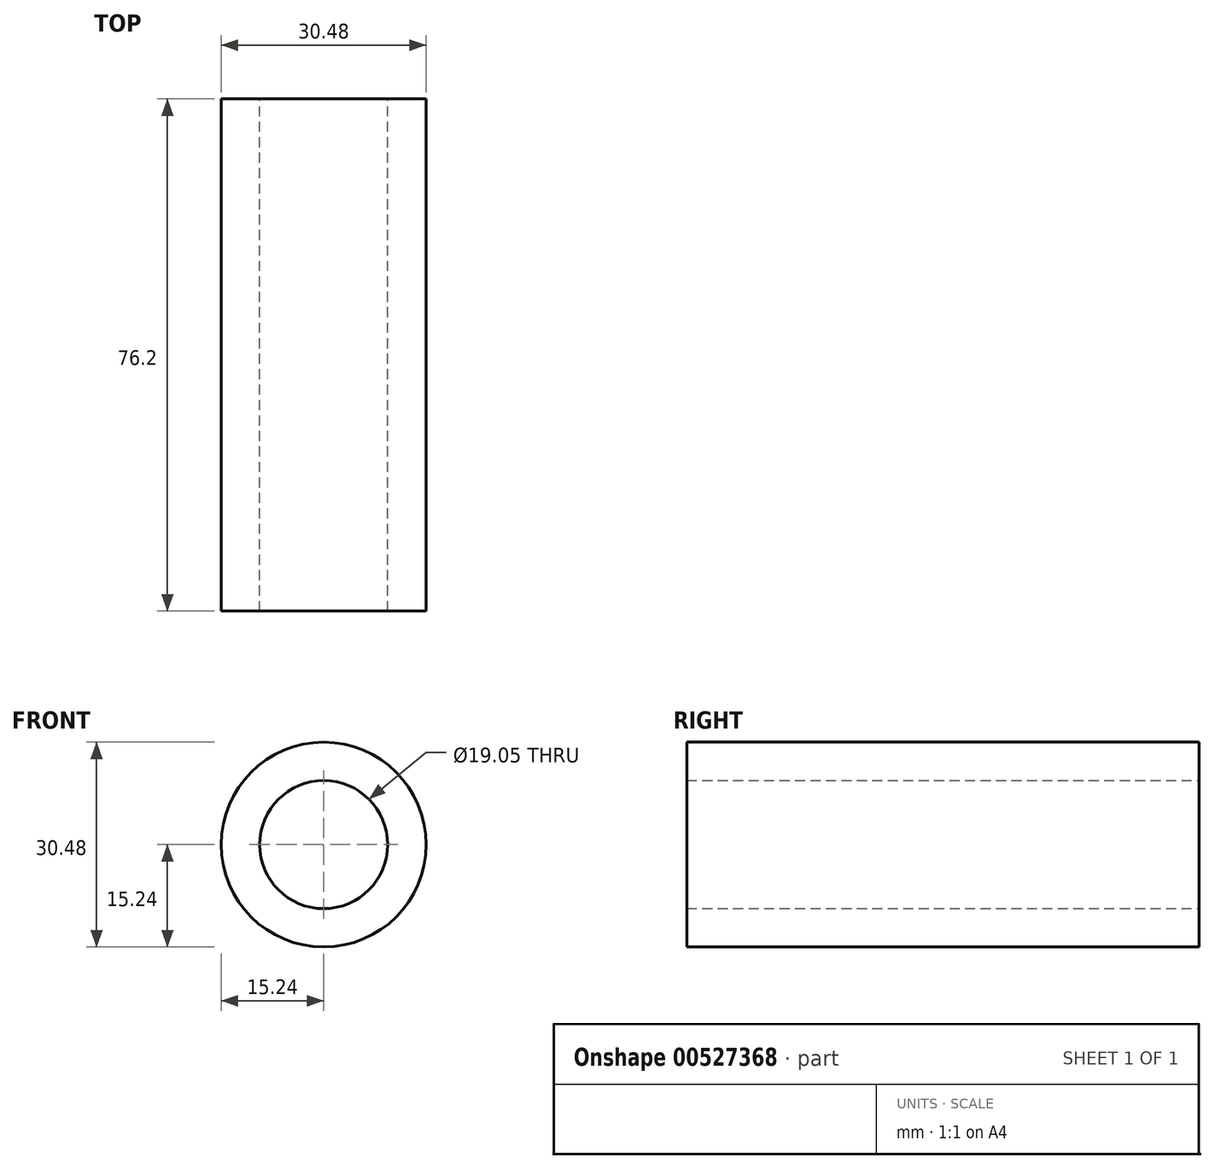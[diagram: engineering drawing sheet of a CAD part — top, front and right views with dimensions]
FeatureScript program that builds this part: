
annotation { "Feature Type Name" : "Feature", "Feature Type Description" : "" }
export const myFeature = defineFeature(function(context is Context, id is Id, definition is map)
    precondition{}
    {
        {
            var Q0;
            Q0=qCreatedBy(makeId("Front.planeOp"),FACE);
            var sketch = newSketch(context, id + "F0", { "sketchPlane" : qUnion([Q0])});
            skCircle(sketch, "E0", {"center": v(0, 0) * mm, "radius": 15.24 * mm});
            skCircle(sketch, "E1", {"center": v(0, 0) * mm, "radius": 9.53 * mm});
            skSolve(sketch);
        }
        {
            var Q0;
            Q0 = qSketchRegion(id + "F0", true);
            extrude(context, id + "F1", {"entities" : qUnion([Q0]), "depth" : 76.2 * mm, "offsetDistance" : 25.4 * mm});
        }
    });
